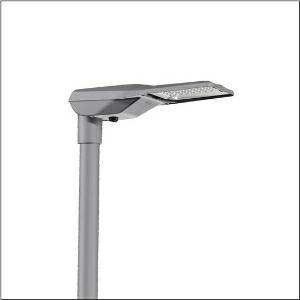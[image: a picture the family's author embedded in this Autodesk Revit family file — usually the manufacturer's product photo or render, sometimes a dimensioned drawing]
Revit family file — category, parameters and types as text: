
# Revit family: streetlight_sl_21_mini___st1_0a_5xe2d33r08hb_bda5
name_source: partatom
category: Lighting Fixtures
units: mm (PartAtom-declared; Revit-internal decimal feet)

## family parameters
Cut with Voids When Loaded = No
Host = Face
Light Source = No
Part Type = Normal
Room Calculation Point = No
Round Connector Dimension = Use Diameter
Shared = No

## types (1)
- --- (1 x LED, 9040 lm, 66 W, 3000K)
    Apparent Load = 66 VA
    CIE Flux Codes = 37 72 97 100 100
    Color Rendering = 70
    Color Temperature = 3000K
    Default Elevation = 1800 mm
    Description = Streetlight SL 21 mini, mast luminaire, primary light control with lens, of PMMA, primary optical cover: cover, of toughened safety glass, transparent, light distribution: ST1.0a, light emission: direct distribution, primary light characteristic: asymmetric, installation type: side-entry, post-top, LED, High Power LED, rated luminous flux: 9.040lm, luminous efficacy: 137lm/W, light colour: 730, colour temperature: 3000K, control gear: ECG Smart Interface, control: flexible luminous flux parameterisation, time-dependent luminous flux control, constant luminous flux control, overheat protection, mains connection: 220..240V, AC, 50/60Hz, start of lifetime: 66W, end of lifetime: 69W, reduction: 30W, luminaire housing, of diecast aluminium, powder-coated, Siteco® metallic grey (DB 702S), corrosivity category C5 according to DIN EN ISO 12944, length: 628mm, width: 235mm, height: 110mm, spigot size: 60/76mm (post-top) and 42/60/76mm (side-entry), mast flange for spigot size: 42mm: 5XC10008XM4, 60mm: 5XC10008XM2, 76/60mm: 5XC10108XM1, protection rating (complete): IP66, insulation class (complete): insulation class II (safety insulation), certification: CE, ENEC, VDE, impact resistance: IK09, permissible operating ambient temperature for outdoor applications: -40..+50°C, standard-compliant lighting for roads and squares, packaging unit: 1 piece

Light Distribution: ST1.0a
    Height = 110 mm
    Lamp = 1 x LED
    Lamp Light Flux = 9040 lm
    Lamp Power = 66 W
    Lamp count = 1
    Length = 625 mm
    Luminous efficacy = 137 lm/W
    Manufacturer = Siteco
    ModVariant = No
    Model = 5XE2D33R08HB
    Number of Poles = 1
    OnlyDefault = Yes
    Power Factor = 1
    Product Name = Streetlight SL 21 mini | ST1.0a
    Product group = mast luminaire | pylon top
    ProductGroupID = 6100
    Protection Class = Protection class II
    Protection Degree = IP 66
    RLX_Detail_Level = 1
    RlxData = <blob elided: 91753 chars, md5=8862ce31>
    Socket = socket
    Standby Power = 0 W
    System Light Flux = 9040 lm
    System Power = 66 W
    Type Comments = factory setting: luminous flux: 100 % | dim-lin: 254 | 670 mA
    Type Image = l_1003516.jpg
    URL = http://relux.com
    VarID = @adj_107037
    Voltage = 0 V
    Weight = 0.00 kg
    Width = 234 mm

## geometry (parser evidence)
native form markers: Blend x4, Sweep x11
no freeform markers — native parametric forms only
